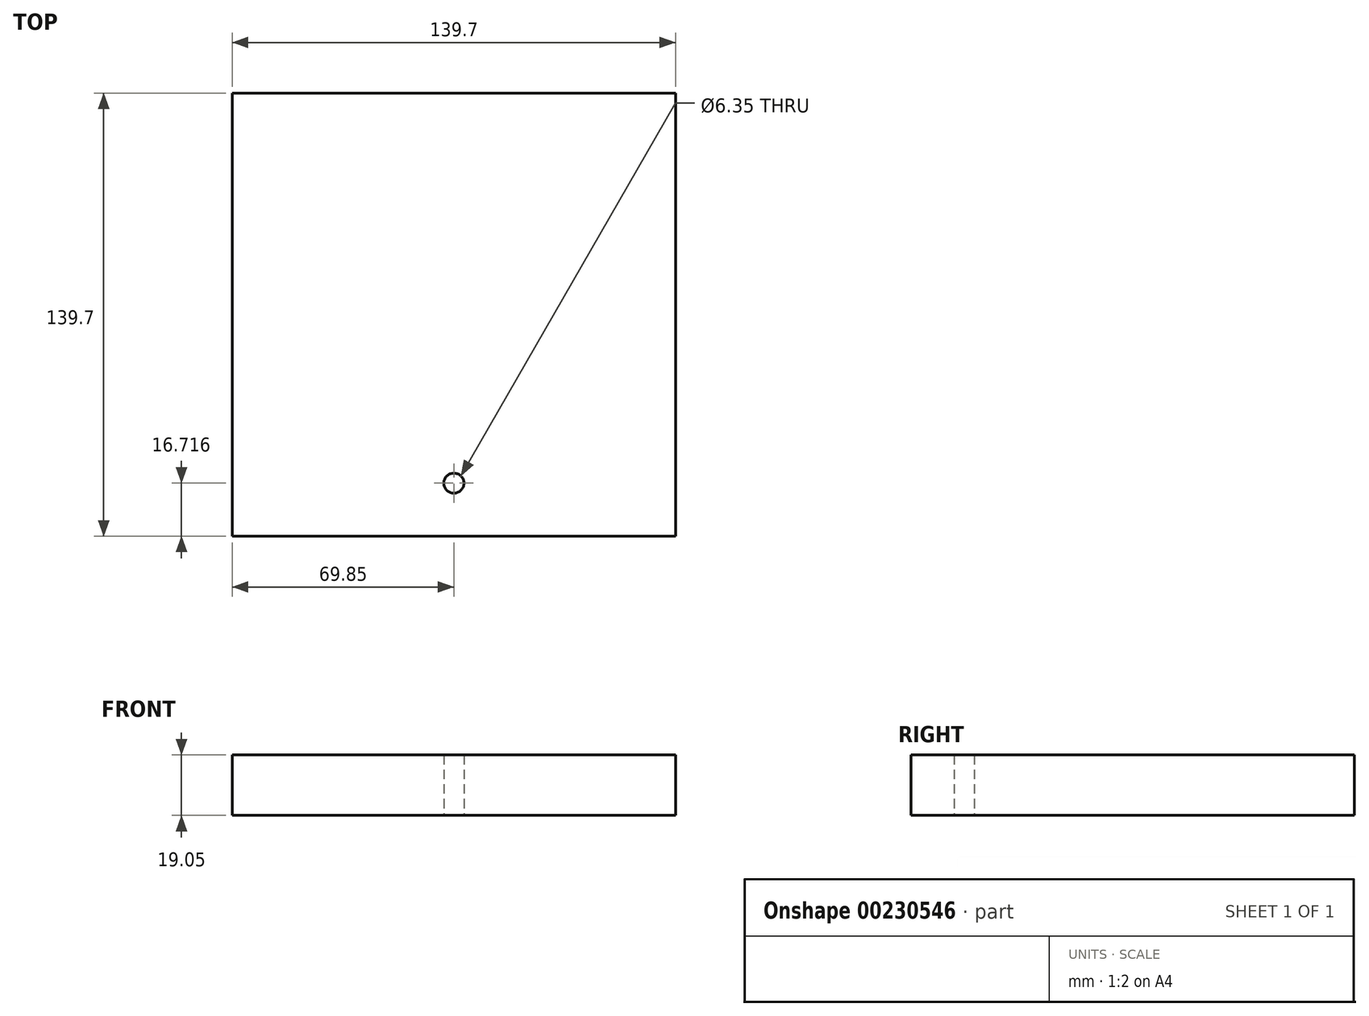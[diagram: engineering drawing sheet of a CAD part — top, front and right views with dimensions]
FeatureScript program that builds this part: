
annotation { "Feature Type Name" : "Feature", "Feature Type Description" : "" }
export const myFeature = defineFeature(function(context is Context, id is Id, definition is map)
    precondition{}
    {
        {
            var Q0;
            Q0=qCreatedBy(makeId("Top.planeOp"),FACE);
            var sketch = newSketch(context, id + "F0", { "sketchPlane" : qUnion([Q0])});
            skLineSegment(sketch, "E0.bottom", {"start": v(-69.85, 69.85) * mm, "end": v(69.85, 69.85) * mm});
            skLineSegment(sketch, "E0.top", {"start": v(-69.85, -69.85) * mm, "end": v(69.85, -69.85) * mm});
            skLineSegment(sketch, "E0.left", {"start": v(-69.85, 69.85) * mm, "end": v(-69.85, -69.85) * mm});
            skLineSegment(sketch, "E0.right", {"start": v(69.85, 69.85) * mm, "end": v(69.85, -69.85) * mm});
            skPoint(sketch, "E0.middle", {"position": v(0, 0) * mm});
            skCircle(sketch, "E1", {"center": v(0, -53.13) * mm, "radius": 3.18 * mm});
            skSolve(sketch);
        }
        {
            var Q0;
            Q0=makeQuery(id+"F0.imprint","IMPRINT",FACE,{"disambiguationData":[TD([[makeQuery(id+"F0.imprint","IMPRINT",EDGE,{"derivedFrom":sQuery(id+"F0.wireOp",EDGE,"E0.bottom")}),-1.0]])]});
            extrude(context, id + "F1", {"entities" : qUnion([Q0]), "depth" : 19.05 * mm});
        }
    });
